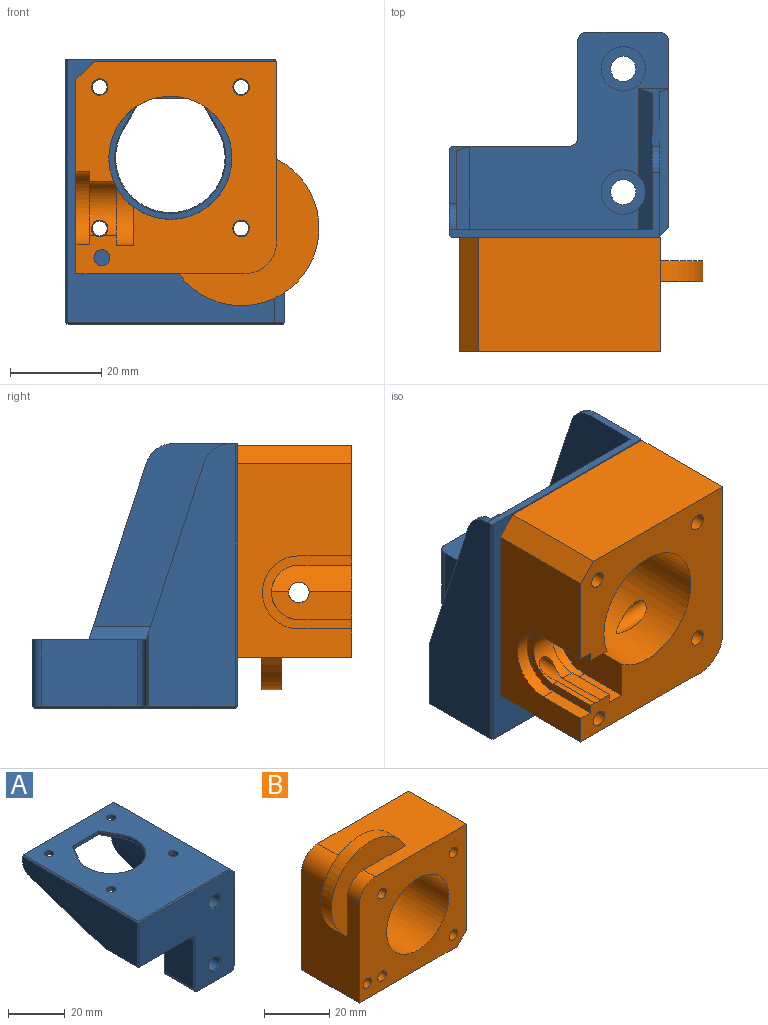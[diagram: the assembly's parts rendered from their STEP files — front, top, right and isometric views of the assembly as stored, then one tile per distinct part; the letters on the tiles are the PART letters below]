
ASSEMBLY  parts=2 mates=1
PART A: 60 faces, bbox 48.2x58x45 mm
  f0: plane 43.6x43.4mm, normal (0,1,0), area 954.4mm2, adj f1,f3,f5,f19,f20,f27,f28,f29
  f1: plane 25.7x14.6mm, normal (0,0,-1), area 375.2mm2, adj f0,f4,f38,f42,f55
  f2: plane 57.6x45.4mm, normal (0,0,1), area 2086.3mm2, adj f6,f14,f15,f16,f17,f18,f21,f22
  f3: plane 43x43mm, normal (0,0,-1), area 1311.3mm2, adj f0,f6,f9,f10,f14,f15,f16,f17
  f4: plane 38.86x12.65mm, normal (0,0.31,-0.95), area 69.7mm2, adj f1,f8,f9,f19,f42,f58
  f5: plane 38.86x12.65mm, normal (0,0.31,-0.95), area 72.2mm2, adj f0,f7,f10,f20,f31,f59
  f6: plane 46.2x14.26mm, normal (0,1,0), area 94.1mm2, adj f2,f3,f7,f8,f9,f10,f30,f43
  f7: plane 41x31.67mm, normal (1,0,0), area 1021.2mm2, adj f5,f6,f30,f31,f59
  f8: plane 57.6x19mm, normal (-1,0,0), area 811mm2, adj f4,f6,f42,f43,f52,f58
  f9: plane 40x17.42mm, normal (1,0,0), area 432.9mm2, adj f3,f4,f6,f19,f58
  f10: plane 40x30.04mm, normal (-1,0,0), area 937.7mm2, adj f3,f5,f6,f20,f59
  f11: plane 7x4.04mm, normal (0.87,-0.5,0), area 9.7mm2, adj f12,f14,f23,f24
  f12: cylinder r=12mm len=24mm, axis (0,0,1), area 60.3mm2, adj f11,f13,f22,f25
  f13: plane 7x4.04mm, normal (-0.87,-0.5,0), area 9.7mm2, adj f12,f14,f21,f26
  f14: plane 13.16x1.6mm, normal (0,-1,0), area 20.4mm2, adj f2,f3,f11,f13,f21,f23,f24,f26
  f15: cylinder r=1.65mm len=3.3mm, axis (0,0,1), area 16.6mm2, adj f2,f3
  f16: cylinder r=1.65mm len=3.3mm, axis (0,0,1), area 16.6mm2, adj f2,f3
  f17: cylinder r=1.65mm len=3.3mm, axis (0,0,1), area 16.6mm2, adj f2,f3
  f18: cylinder r=1.65mm len=3.3mm, axis (0,0,1), area 16.6mm2, adj f2,f3
  f19: plane 18.4x3mm, normal (0.71,0.71,0), area 76mm2, adj f0,f3,f4,f9
  f20: plane 31.02x3mm, normal (-0.71,0.71,0), area 119.5mm2, adj f0,f3,f5,f10,f37
  f21: plane 7x4.21mm, normal (-0.61,-0.35,0.71), area 2.3mm2, adj f2,f13,f14,f22
  f22: cone r=12mm half-angle=45deg, axis (0,0,1), area 14.3mm2, adj f2,f12,f21,f23
  f23: plane 7x4.21mm, normal (0.61,-0.35,0.71), area 2.3mm2, adj f2,f11,f14,f22
  f24: plane 7x4.21mm, normal (0.61,-0.35,-0.71), area 2.3mm2, adj f3,f11,f14,f25
  f25: cone r=12mm half-angle=45deg, axis (0,0,-1), area 14.3mm2, adj f3,f12,f24,f26
  f26: plane 7x4.21mm, normal (-0.61,-0.35,-0.71), area 2.3mm2, adj f3,f13,f14,f25
  f27: plane 21x14.6mm, normal (-1,0,0), area 306.6mm2, adj f0,f38,f39,f51
  f28: plane 16x14.6mm, normal (0,0,-1), area 233.6mm2, adj f0,f39,f40,f47
  f29: plane 40.7x14.6mm, normal (1,0,0), area 594.2mm2, adj f0,f30,f31,f40,f44
  f30: plane 57.6x2.3mm, normal (0.71,0,0.71), area 68.6mm2, adj f2,f6,f7,f29,f31,f46
  f31: plane 32.32x2mm, normal (0.71,0.71,0), area 87.7mm2, adj f5,f7,f29,f30
  f32: cylinder r=2.75mm len=5.5mm, axis (0,1,0), area 86.4mm2, adj f33,f57
  f33: plane 9.75x9.75mm, normal (0,1,0), area 50.9mm2, adj f32,f34
  f34: cylinder r=4.88mm len=9.75mm, axis (0,1,0), area 294.1mm2, adj f0,f33
  f35: cylinder r=2.75mm len=5.5mm, axis (0,1,0), area 86.4mm2, adj f36,f56
  f36: plane 9.75x9.75mm, normal (0,1,0), area 50.9mm2, adj f35,f37
  f37: cylinder r=4.88mm len=11.08mm, axis (0,1,0), area 301.6mm2, adj f0,f20,f36
  f38: cylinder r=2mm len=14.6mm, axis (0,-1,0), area 45.9mm2, adj f0,f1,f27,f53
  f39: cylinder r=2mm len=14.6mm, axis (0,-1,0), area 45.9mm2, adj f0,f27,f28,f49
  f40: cylinder r=2mm len=14.6mm, axis (0,1,0), area 45.9mm2, adj f0,f28,f29,f45
  f41: plane 47.4x44.2mm, normal (0,-1,0), area 1325.7mm2, adj f44,f45,f46,f47,f48,f49,f50,f51
  f42: plane 16.14x0.5mm, normal (-0.71,0,-0.71), area 10.9mm2, adj f1,f4,f8,f54
  f43: plane 57.6x0.5mm, normal (-0.71,0,0.71), area 40.7mm2, adj f2,f6,f8,f50
  f44: plane 40.7x0.4mm, normal (0.71,-0.71,0), area 23mm2, adj f29,f41,f45,f46
  f45: cone r=1.6mm half-angle=45deg, axis (0,1,0), area 1.6mm2, adj f40,f41,f44,f47
  f46: plane 2.47x2.47mm, normal (0.5,-0.71,0.5), area 1.7mm2, adj f30,f41,f44,f48
  f47: plane 16x0.4mm, normal (0,-0.71,-0.71), area 9.1mm2, adj f28,f41,f45,f49
  f48: plane 45.4x0.4mm, normal (0,-0.71,0.71), area 25.6mm2, adj f2,f41,f46,f50
  f49: cone r=1.6mm half-angle=45deg, axis (0,1,0), area 1.6mm2, adj f39,f41,f47,f51
  f50: plane 0.67x0.67mm, normal (-0.5,-0.71,0.5), area 0.3mm2, adj f41,f43,f48,f52
  f51: plane 21x0.4mm, normal (-0.71,-0.71,0), area 11.9mm2, adj f27,f41,f49,f53
  f52: plane 19x0.4mm, normal (-0.71,-0.71,0), area 10.7mm2, adj f8,f41,f50,f54
  f53: cone r=2.4mm half-angle=45deg, axis (0,-1,0), area 2mm2, adj f38,f41,f51,f55
  f54: plane 0.67x0.67mm, normal (-0.5,-0.71,-0.5), area 0.3mm2, adj f41,f42,f52,f55
  f55: plane 25.7x0.4mm, normal (0,-0.71,-0.71), area 14.5mm2, adj f1,f41,f53,f54
  f56: cone r=2.75mm half-angle=45deg, axis (0,-1,0), area 10.5mm2, adj f35,f41
  f57: cone r=2.75mm half-angle=45deg, axis (0,-1,0), area 10.5mm2, adj f32,f41
  f58: cylinder r=6mm len=5.71mm, axis (-1,0,0), area 12.1mm2, adj f4,f6,f8,f9
  f59: cylinder r=6mm len=5.71mm, axis (-1,0,0), area 12.1mm2, adj f5,f6,f7,f10
PART B: 32 faces, bbox 53.5x25x53.3 mm
  f0: cylinder r=1.8mm len=25mm, axis (0,1,0), area 282.7mm2, adj f10,f17
  f1: cylinder r=1.8mm len=25mm, axis (0,1,0), area 135.4mm2, adj f8,f10,f11,f17,f27
  f2: cylinder r=1.8mm len=25mm, axis (0,1,0), area 282.7mm2, adj f10,f17
  f3: cylinder r=1.8mm len=25mm, axis (0,1,0), area 282.7mm2, adj f10,f17
  f4: cylinder r=1.75mm len=25mm, axis (0,1,0), area 274.9mm2, adj f10,f17
  f5: cylinder r=13.5mm len=27mm, axis (0,-1,0), area 1942.5mm2, adj f6,f7,f10,f11,f17,f23,f24,f25
  f6: cylinder r=2.25mm len=5.99mm, axis (0,0,-1), area 22.5mm2, adj f5,f23
  f7: cylinder r=2.25mm len=21.3mm, axis (0,0,-1), area 230.5mm2, adj f5,f15
  f8: plane 11.57x1.38mm, normal (1,0,0), area 15.9mm2, adj f1,f10,f11,f12
  f9: plane 42.5x25mm, normal (0,0,-1), area 776.9mm2, adj f10,f13,f16,f17,f26,f30,f31
  f10: plane 46.5x44mm, normal (0,1,0), area 1257.6mm2, adj f0,f1,f2,f3,f4,f5,f8,f9
  f11: cylinder r=6mm len=12mm, axis (0,0,-1), area 91.5mm2, adj f1,f5,f8,f12,f25,f27,f29
  f12: plane 19.57x16mm, normal (0,0,-1), area 90.2mm2, adj f8,f10,f11,f13,f26,f29,f30
  f13: cylinder r=8mm len=16mm, axis (0,0,-1), area 75.4mm2, adj f9,f12,f26,f30
  f14: cylinder r=7mm len=7mm, axis (0,1,0), area 56.4mm2, adj f15,f16,f17,f22
  f15: plane 39.5x25mm, normal (0,0,1), area 890mm2, adj f7,f10,f14,f17,f18,f19,f20,f21
  f16: plane 37x25mm, normal (-1,0,0), area 859.9mm2, adj f9,f10,f14,f17,f19,f20,f21,f22
  f17: plane 46.5x44mm, normal (0,-1,0), area 1404.6mm2, adj f0,f1,f2,f3,f4,f5,f9,f14
  f18: plane 40x25mm, normal (1,0,0), area 1000mm2, adj f10,f15,f17,f31
  f19: cylinder r=7mm len=15.37mm, axis (0,1,0), area 169mm2, adj f10,f15,f16,f21
  f20: cylinder r=17mm len=32.15mm, axis (0,-1,0), area 276.4mm2, adj f15,f16,f21,f22
  f21: plane 32.15x30.76mm, normal (0,1,0), area 328.5mm2, adj f15,f16,f19,f20
  f22: plane 32.15x30.76mm, normal (0,-1,0), area 328.5mm2, adj f14,f15,f16,f20
  f23: plane 19.67x8.33mm, normal (0,0,-1), area 140.7mm2, adj f5,f6,f10,f24,f28
  f24: cylinder r=8.1mm len=12.64mm, axis (0,0,-1), area 57.9mm2, adj f5,f23,f25,f28
  f25: plane 19.67x12.64mm, normal (0,0,1), area 57.9mm2, adj f5,f10,f11,f24,f27,f28
  f26: plane 11.57x3mm, normal (1,0,0), area 34.7mm2, adj f9,f10,f12,f13
  f27: plane 11.57x2.88mm, normal (1,0,0), area 33.3mm2, adj f1,f10,f11,f25
  f28: plane 11.57x3.8mm, normal (1,0,0), area 44mm2, adj f10,f23,f24,f25
  f29: plane 11.57x5.2mm, normal (-1,0,0), area 60.2mm2, adj f5,f10,f11,f12
  f30: plane 11.57x3mm, normal (-1,0,0), area 34.7mm2, adj f9,f10,f12,f13
  f31: plane 25x4mm, normal (0.71,0,-0.71), area 141.4mm2, adj f9,f10,f17,f18
PLACE A rot(axis=(1,0,0),90deg) t=(23.97,-6.7,65.86)mm
PLACE B rot(axis=(-0.71,0,-0.71),180deg) t=(3.27,-20.13,54.76)mm
MATE fastened B.f3 <-> A.f18  axis (0,1,0) through (39.47,-6.7,81.36)mm
